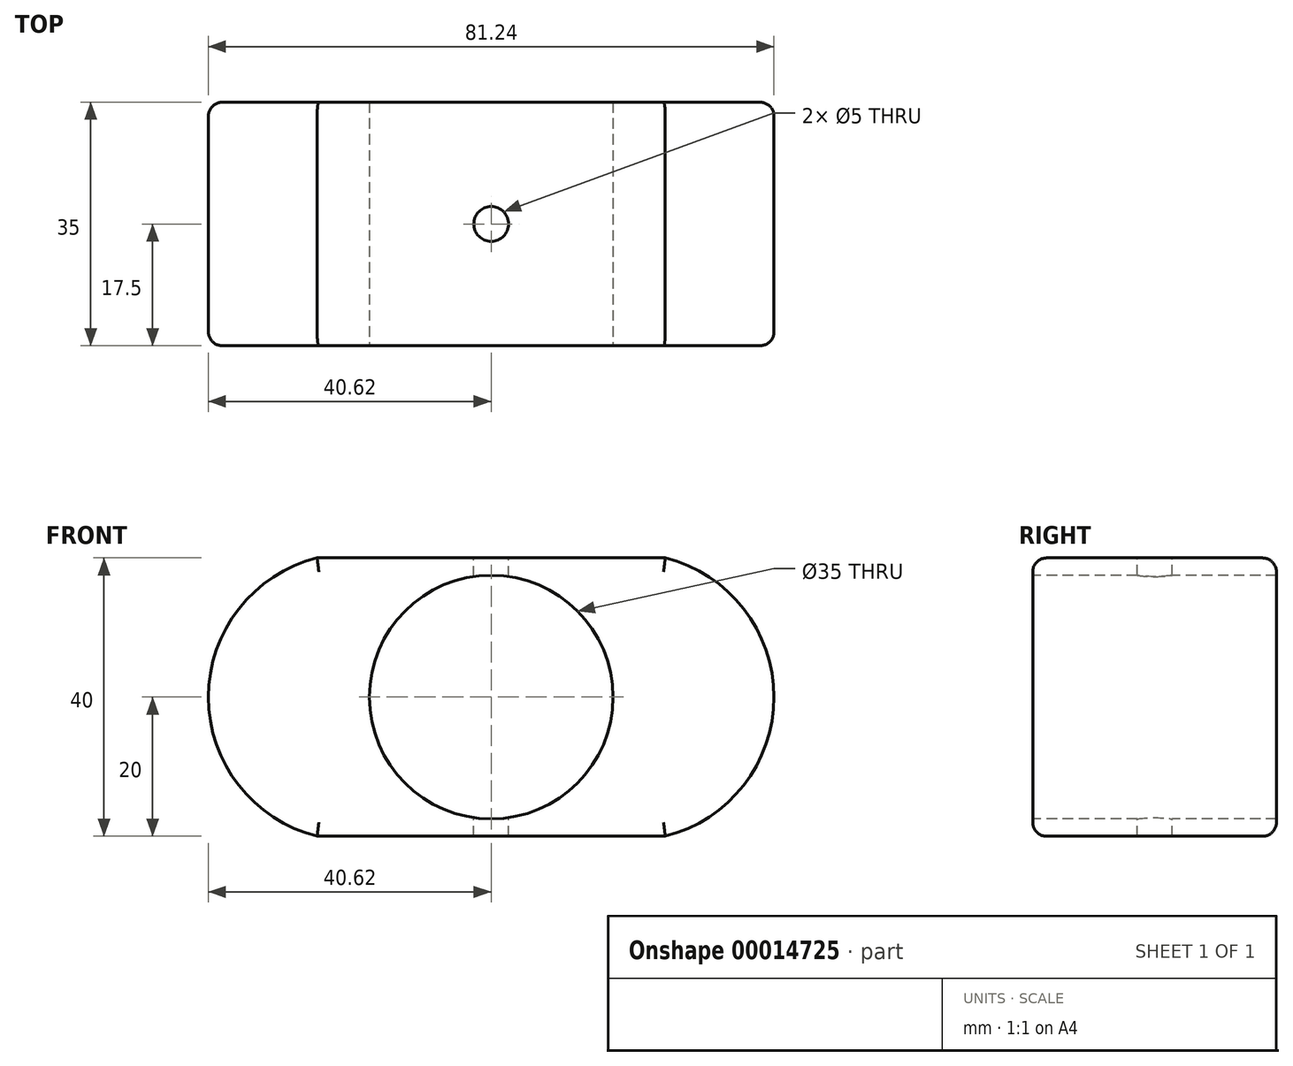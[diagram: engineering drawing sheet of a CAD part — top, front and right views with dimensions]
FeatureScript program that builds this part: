
annotation { "Feature Type Name" : "Feature", "Feature Type Description" : "" }
export const myFeature = defineFeature(function(context is Context, id is Id, definition is map)
    precondition{}
    {
        {
            var Q0;
            Q0=qCreatedBy(makeId("Front.planeOp"),FACE);
            var sketch = newSketch(context, id + "F0", { "sketchPlane" : qUnion([Q0])});
            skLineSegment(sketch, "E0.bottom", {"start": v(0, 0) * mm, "end": v(-50, 0) * mm});
            skLineSegment(sketch, "E0.top", {"start": v(0, 40) * mm, "end": v(-50, 40) * mm});
            skLineSegment(sketch, "E0.left", {"start": v(0, 0) * mm, "end": v(0, 40) * mm});
            skLineSegment(sketch, "E0.right", {"start": v(-50, 0) * mm, "end": v(-50, 40) * mm});
            skArc(sketch, "E1", {"start": v(0, 0) * mm, "mid": v(15.62, 20) * mm, "end": v(0, 40) * mm});
            skArc(sketch, "E2", {"start": v(-50, 40) * mm, "mid": v(-65.62, 20) * mm, "end": v(-50, 0) * mm});
            skSolve(sketch);
        }
        {
            var Q0;
            Q0=qSketchRegion(id+"F0",true);
            extrude(context, id + "F1", {"entities" : qUnion([Q0]), "depth" : 35 * mm});
        }
        {
            var Q0;
            Q0=makeQuery(id+"F1.opExtrude","CAP_FACE",FACE,{"disambiguationData":[OSD([sQuery(id+"F0.wireOp",EDGE,"E0.bottom"),sQuery(id+"F0.wireOp",EDGE,"E0.top"),sQuery(id+"F0.wireOp",EDGE,"E1"),sQuery(id+"F0.wireOp",EDGE,"E2")])],"isStart":false});
            var sketch = newSketch(context, id + "F2", { "sketchPlane" : qUnion([Q0])});
            skCircle(sketch, "E3", {"center": v(-25, 20) * mm, "radius": 17.5 * mm});
            skSolve(sketch);
        }
        {
            var Q0;
            Q0=qSketchRegion(id+"F2",true);
            extrude(context, id + "F3", {"entities" : qUnion([Q0]), "operationType" : NewBodyOperationType.REMOVE, "oppositeDirection" : true, "depth" : 35 * mm});
        }
        {
            var Q0;
            Q0=makeQuery(id+"F1.opExtrude","SWEPT_FACE",FACE,{"disambiguationData":[OSD([sQuery(id+"F0.wireOp",EDGE,"E0.top")])]});
            var sketch = newSketch(context, id + "F4", { "sketchPlane" : qUnion([Q0])});
            skCircle(sketch, "E4", {"center": v(-25, -17.5) * mm, "radius": 2.5 * mm});
            skSolve(sketch);
        }
        {
            var Q0;
            Q0=qSketchRegion(id+"F4",true);
            extrude(context, id + "F5", {"entities" : qUnion([Q0]), "operationType" : NewBodyOperationType.REMOVE, "endBound" : BoundingType.THROUGH_ALL, "oppositeDirection" : true, "depth" : 25 * mm});
        }
        {
            var Q0;
            Q0=makeQuery(id+"F1.opExtrude","CAP_EDGE",EDGE,{"disambiguationData":[OSD([sQuery(id+"F0.wireOp",EDGE,"E0.top")])],"isStart":false});
            var Q1;
            Q1=makeQuery(id+"F1.opExtrude","CAP_EDGE",EDGE,{"disambiguationData":[OSD([sQuery(id+"F0.wireOp",EDGE,"E0.bottom")])],"isStart":false});
            var Q2;
            Q2=makeQuery(id+"F1.opExtrude","CAP_EDGE",EDGE,{"disambiguationData":[OSD([sQuery(id+"F0.wireOp",EDGE,"E2")])],"isStart":false});
            var Q3;
            Q3=makeQuery(id+"F1.opExtrude","CAP_EDGE",EDGE,{"disambiguationData":[OSD([sQuery(id+"F0.wireOp",EDGE,"E1")])],"isStart":false});
            var Q4;
            Q4=makeQuery(id+"F1.opExtrude","CAP_EDGE",EDGE,{"disambiguationData":[OSD([sQuery(id+"F0.wireOp",EDGE,"E0.top")])],"isStart":true});
            var Q5;
            Q5=makeQuery(id+"F1.opExtrude","CAP_EDGE",EDGE,{"disambiguationData":[OSD([sQuery(id+"F0.wireOp",EDGE,"E2")])],"isStart":true});
            var Q6;
            Q6=makeQuery(id+"F1.opExtrude","CAP_EDGE",EDGE,{"disambiguationData":[OSD([sQuery(id+"F0.wireOp",EDGE,"E1")])],"isStart":true});
            var Q7;
            Q7=makeQuery(id+"F1.opExtrude","CAP_EDGE",EDGE,{"disambiguationData":[OSD([sQuery(id+"F0.wireOp",EDGE,"E0.bottom")])],"isStart":true});
            fillet(context, id + "F6", {"entities" : qUnion([Q0, Q1, Q2, Q3, Q4, Q5, Q6, Q7]), "radius" : 2 * mm, "tangentPropagation" : true, "allowEdgeOverflow" : false});
        }
    });
